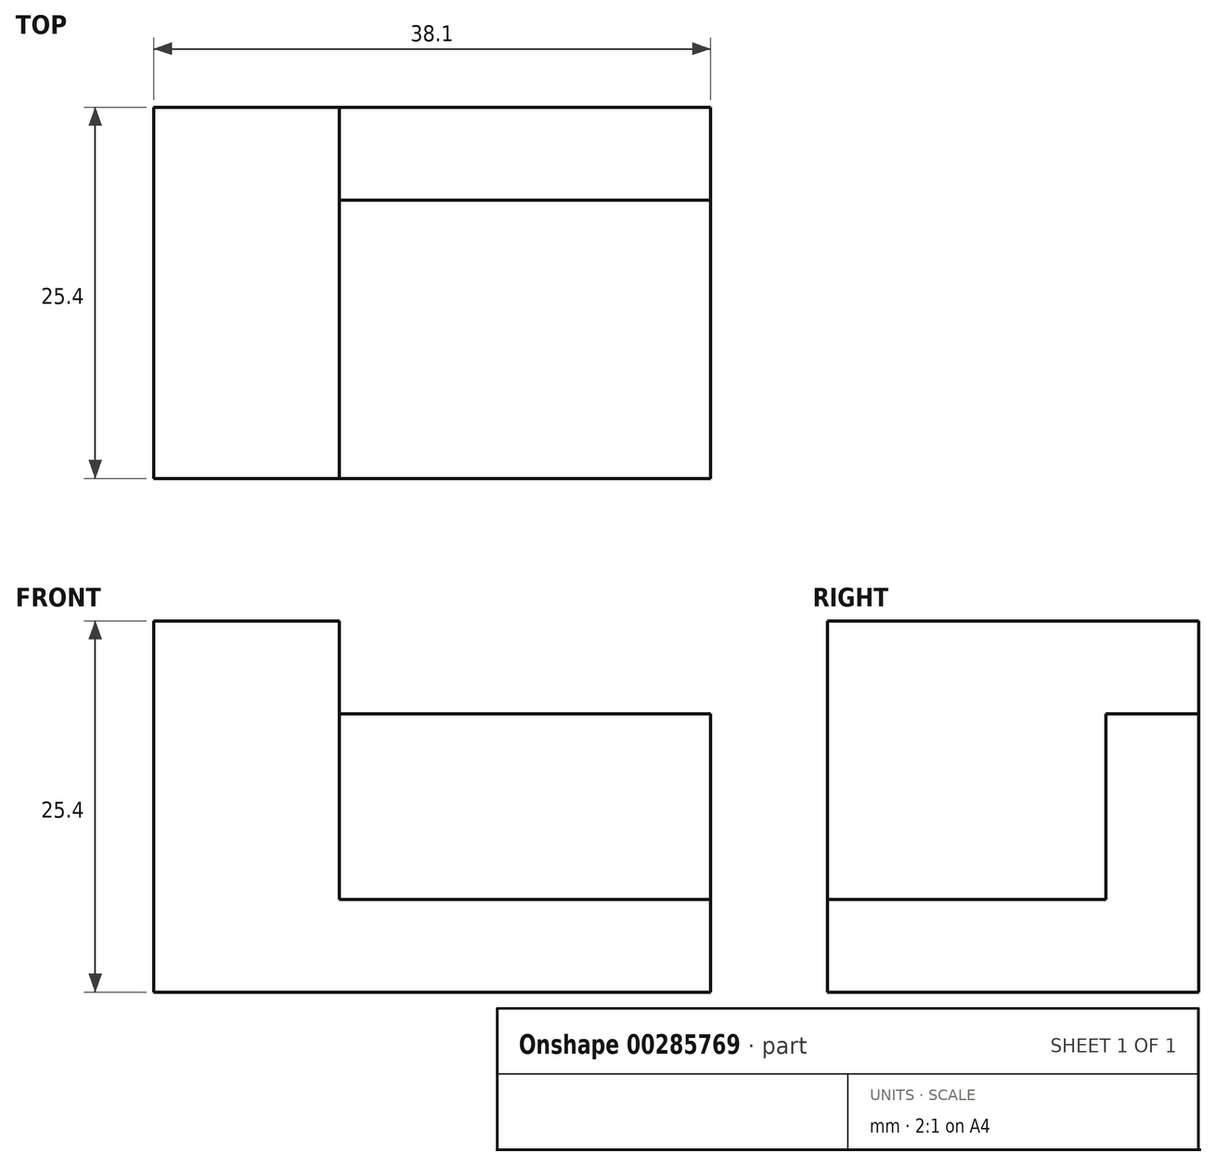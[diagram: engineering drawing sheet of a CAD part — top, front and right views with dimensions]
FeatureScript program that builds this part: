
annotation { "Feature Type Name" : "Feature", "Feature Type Description" : "" }
export const myFeature = defineFeature(function(context is Context, id is Id, definition is map)
    precondition{}
    {
        {
            var Q0;
            Q0=qCreatedBy(makeId("Front.planeOp"),FACE);
            var sketch = newSketch(context, id + "F0", { "sketchPlane" : qUnion([Q0])});
            skLineSegment(sketch, "E0", {"start": v(0, 0) * mm, "end": v(38.1, 0) * mm});
            skLineSegment(sketch, "E1", {"start": v(38.1, 0) * mm, "end": v(38.1, 6.35) * mm});
            skLineSegment(sketch, "E2", {"start": v(38.1, 6.35) * mm, "end": v(12.7, 6.35) * mm});
            skLineSegment(sketch, "E3", {"start": v(12.7, 6.35) * mm, "end": v(12.7, 25.4) * mm});
            skLineSegment(sketch, "E4", {"start": v(12.7, 25.4) * mm, "end": v(0, 25.4) * mm});
            skLineSegment(sketch, "E5", {"start": v(0, 25.4) * mm, "end": v(0, 0) * mm});
            skLineSegment(sketch, "E6", {"start": v(12.7, 6.35) * mm, "end": v(12.7, 0) * mm});
            skSolve(sketch);
        }
        {
            var Q0;
            {var subQ0=sQuery(id+"F0.wireOp",EDGE,"E1");Q0=makeQuery(id+"F0.imprint","IMPRINT",FACE,{"disambiguationData":[TD([[makeQuery(id+"F0.imprint","IMPRINT",EDGE,{"derivedFrom":subQ0}),1.0]])]});}
            extrude(context, id + "F1", {"entities" : qUnion([Q0]), "oppositeDirection" : true, "depth" : 19.05 * mm});
        }
        {
            var Q0;
            Q0=makeQuery(id+"F0.imprint","IMPRINT",FACE,{"disambiguationData":[TD([[makeQuery(id+"F0.imprint","IMPRINT",EDGE,{"derivedFrom":sQuery(id+"F0.wireOp",EDGE,"E3")}),1.0]])]});
            extrude(context, id + "F2", {"entities" : qUnion([Q0]), "operationType" : NewBodyOperationType.ADD, "oppositeDirection" : true, "depth" : 25.4 * mm});
        }
        {
            var Q0;
            Q0=makeQuery(id+"F2.opExtrude","SWEPT_FACE",FACE,{"disambiguationData":[OSD([sQuery(id+"F0.wireOp",EDGE,"E5")])]});
            var sketch = newSketch(context, id + "F3", { "sketchPlane" : qUnion([Q0])});
            skLineSegment(sketch, "E7", {"start": v(-19.05, 0) * mm, "end": v(-19.05, 25.4) * mm});
            skSolve(sketch);
        }
        {
            var Q0;
            Q0 = qSketchRegion(id + "F3", true);
            var Q1;
            {var subQ0=sQuery(id+"F3.wireOp",EDGE,"E7");Q1=makeQuery(id+"F3.imprint","IMPRINT",FACE,{"disambiguationData":[TD([[makeQuery(id+"F3.imprint","IMPRINT",EDGE,{"derivedFrom":subQ0}),1.0]])]});}
            extrude(context, id + "F4", {"entities" : qUnion([Q0, Q1]), "operationType" : NewBodyOperationType.ADD, "oppositeDirection" : true, "depth" : 38.1 * mm});
        }
        {
            var Q0;
            Q0=makeQuery(id+"F4.boolean.opBoolean","MERGE",FACE,{"derivedFrom":[makeQuery(id+"F1.opExtrude","SWEPT_FACE",FACE,{"disambiguationData":[OSD([sQuery(id+"F0.wireOp",EDGE,"E1")])]}),makeQuery(id+"F4.opExtrude","CAP_FACE",FACE,{"disambiguationData":[OSD([sQuery(id+"F0.wireOp",EDGE,"E0"),sQuery(id+"F0.wireOp",EDGE,"E4"),sQuery(id+"F0.wireOp",EDGE,"E5"),sQuery(id+"F3.wireOp",EDGE,"E7")])],"isStart":false})]});
            var sketch = newSketch(context, id + "F5", { "sketchPlane" : qUnion([Q0])});
            skLineSegment(sketch, "E8", {"start": v(25.4, 19.05) * mm, "end": v(19.05, 19.05) * mm});
            skSolve(sketch);
        }
        {
            var Q0;
            Q0 = qSketchRegion(id + "F5", true);
            var Q1;
            {var subQ0=sQuery(id+"F5.wireOp",EDGE,"E8");Q1=makeQuery(id+"F5.imprint","IMPRINT",FACE,{"disambiguationData":[TD([[makeQuery(id+"F5.imprint","IMPRINT",EDGE,{"derivedFrom":subQ0}),-1.0]])]});}
            extrude(context, id + "F6", {"entities" : qUnion([Q0, Q1]), "operationType" : NewBodyOperationType.REMOVE, "oppositeDirection" : true, "depth" : 25.4 * mm});
        }
    });
